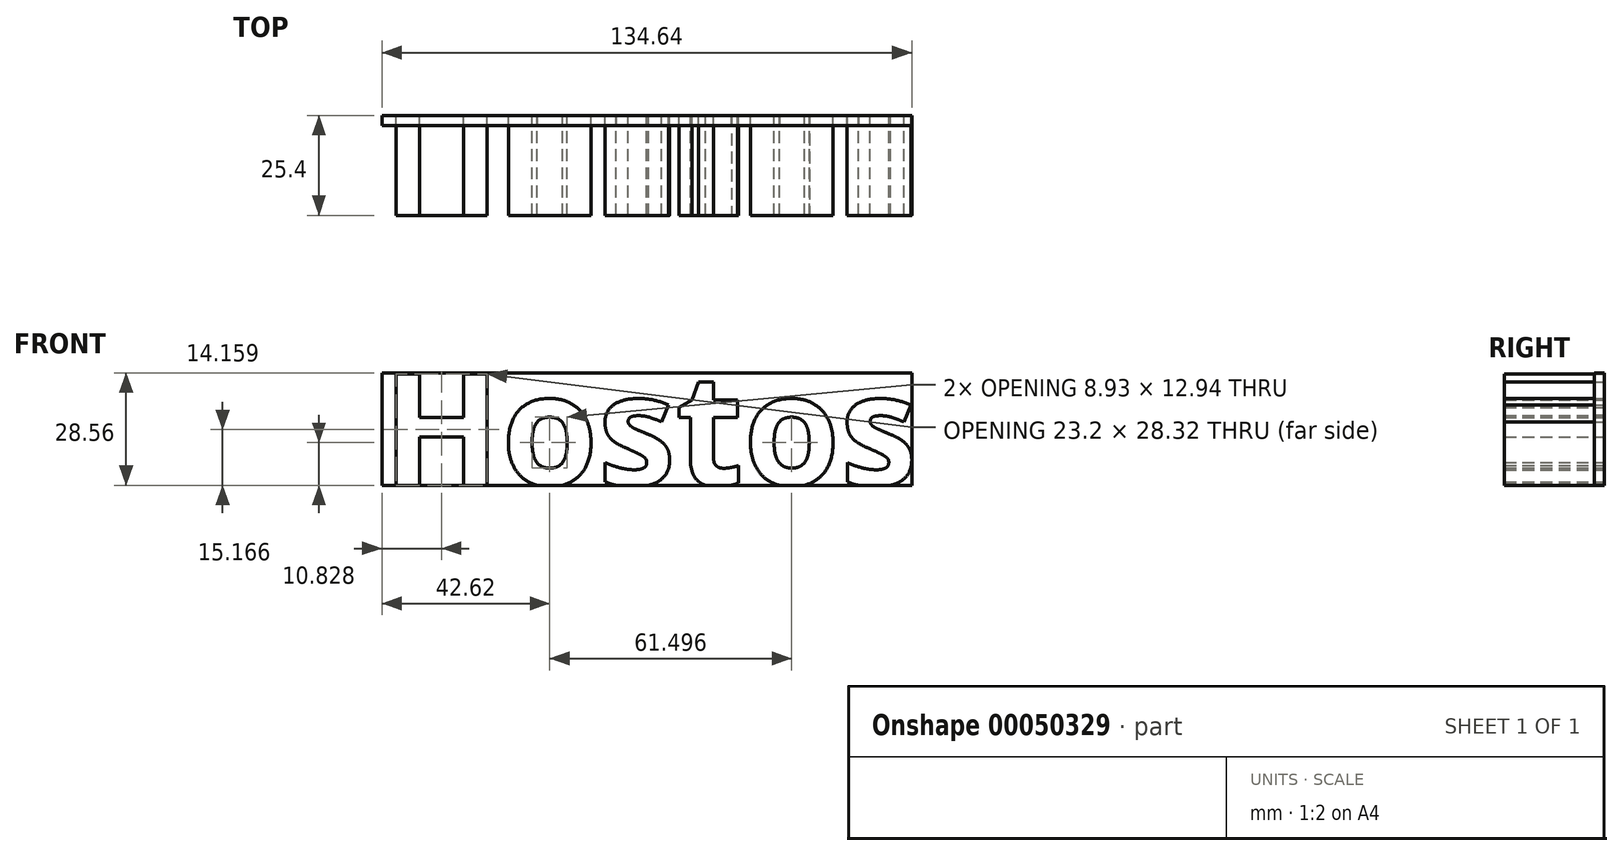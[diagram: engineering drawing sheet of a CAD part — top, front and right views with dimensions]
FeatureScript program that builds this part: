
annotation { "Feature Type Name" : "Feature", "Feature Type Description" : "" }
export const myFeature = defineFeature(function(context is Context, id is Id, definition is map)
    precondition{}
    {
        {
            var Q0;
            Q0=qCreatedBy(makeId("Front.planeOp"),FACE);
            var sketch = newSketch(context, id + "F0", { "sketchPlane" : qUnion([Q0])});
            skText(sketch, "E0", { "text": "Hostos", "fontName": "OpenSans-Bold.ttf"});
            skLineSegment(sketch, "E1.bottom", {"start": v(-52.26, 41.7) * mm, "end": v(82.38, 41.7) * mm});
            skLineSegment(sketch, "E1.top", {"start": v(-52.26, 13.15) * mm, "end": v(82.38, 13.15) * mm});
            skLineSegment(sketch, "E1.left", {"start": v(-52.26, 41.7) * mm, "end": v(-52.26, 13.15) * mm});
            skLineSegment(sketch, "E1.right", {"start": v(82.38, 41.7) * mm, "end": v(82.38, 13.15) * mm});
            skLineSegment(sketch, "E2", {"start": v(-37.26, 25.7) * mm, "end": v(-37.26, 30.35) * mm});
            skLineSegment(sketch, "E3", {"start": v(-14.4, 23.81) * mm, "end": v(-20.07, 23.81) * mm});
            skLineSegment(sketch, "E4", {"start": v(-5.28, 23.64) * mm, "end": v(1.25, 23.64) * mm});
            skLineSegment(sketch, "E5", {"start": v(41.14, 24.33) * mm, "end": v(47.33, 24.33) * mm});
            skLineSegment(sketch, "E6", {"start": v(56.27, 24.5) * mm, "end": v(62.3, 24.5) * mm});
            const initialGuessF0  = {"E0": [-0.05226, 0.01315, 1, 0, 0.02856]};
            skSetInitialGuess(sketch, initialGuessF0);
            skSolve(sketch);
        }
        {
            var Q0;
            {var subQ0=sQuery(id+"F0.wireOp",EDGE,"E0.sketch_text.stroke-1");Q0=makeQuery(id+"F0.imprint","IMPRINT",FACE,{"disambiguationData":[TD([[makeQuery(id+"F0.imprint","IMPRINT",EDGE,{"derivedFrom":subQ0}),-1.0]])]});}
            var Q1;
            Q1=makeQuery(id+"F0.imprint","IMPRINT",FACE,{"disambiguationData":[TD([[makeQuery(id+"F0.imprint","IMPRINT",EDGE,{"derivedFrom":sQuery(id+"F0.wireOp",EDGE,"E0.sketch_text.stroke-12")}),-1.0]])]});
            var Q2;
            {var subQ4=sQuery(id+"F0.wireOp",EDGE,"E0.sketch_text.stroke-30");Q2=makeQuery(id+"F0.imprint","IMPRINT",FACE,{"disambiguationData":[TD([[makeQuery(id+"F0.imprint","IMPRINT",EDGE,{"derivedFrom":subQ4}),-1.0]])]});}
            var Q3;
            Q3=makeQuery(id+"F0.imprint","IMPRINT",FACE,{"disambiguationData":[TD([[makeQuery(id+"F0.imprint","IMPRINT",EDGE,{"derivedFrom":sQuery(id+"F0.wireOp",EDGE,"E0.sketch_text.stroke-56")}),-1.0]])]});
            var Q4;
            Q4=makeQuery(id+"F0.imprint","IMPRINT",FACE,{"disambiguationData":[TD([[makeQuery(id+"F0.imprint","IMPRINT",EDGE,{"derivedFrom":sQuery(id+"F0.wireOp",EDGE,"E0.sketch_text.stroke-74")}),-1.0]])]});
            var Q5;
            {var subQ4=sQuery(id+"F0.wireOp",EDGE,"E0.sketch_text.stroke-92");Q5=makeQuery(id+"F0.imprint","IMPRINT",FACE,{"disambiguationData":[TD([[makeQuery(id+"F0.imprint","IMPRINT",EDGE,{"derivedFrom":subQ4}),-1.0]])]});}
            extrude(context, id + "F1", {"entities" : qUnion([Q0, Q1, Q2, Q3, Q4, Q5]), "depth" : 25.4 * mm});
        }
        {
            var Q0;
            {var subQ25=sQuery(id+"F0.wireOp",EDGE,"E0.sketch_text.stroke-5");Q0=makeQuery(id+"F0.imprint","IMPRINT",FACE,{"disambiguationData":[TD([[makeQuery(id+"F0.imprint","IMPRINT",EDGE,{"derivedFrom":subQ25}),1.0]])]});}
            var Q1;
            {var subQ0=sQuery(id+"F0.wireOp",EDGE,"E0.sketch_text.stroke-1");Q1=makeQuery(id+"F0.imprint","IMPRINT",FACE,{"disambiguationData":[TD([[makeQuery(id+"F0.imprint","IMPRINT",EDGE,{"derivedFrom":subQ0}),1.0]])]});}
            var Q2;
            {var subQ0=sQuery(id+"F0.wireOp",EDGE,"E0.sketch_text.stroke-92");Q2=makeQuery(id+"F0.imprint","IMPRINT",FACE,{"disambiguationData":[TD([[makeQuery(id+"F0.imprint","IMPRINT",EDGE,{"derivedFrom":subQ0}),1.0]])]});}
            var Q3;
            Q3=makeQuery(id+"F0.imprint","IMPRINT",FACE,{"disambiguationData":[TD([[makeQuery(id+"F0.imprint","IMPRINT",EDGE,{"derivedFrom":sQuery(id+"F0.wireOp",EDGE,"E0.sketch_text.stroke-12")}),1.0]])]});
            var Q4;
            Q4=makeQuery(id+"F0.imprint","IMPRINT",FACE,{"disambiguationData":[TD([[makeQuery(id+"F0.imprint","IMPRINT",EDGE,{"derivedFrom":sQuery(id+"F0.wireOp",EDGE,"E0.sketch_text.stroke-74")}),1.0]])]});
            extrude(context, id + "F2", {"entities" : qUnion([Q0, Q1, Q2, Q3, Q4]), "depth" : 2.54 * mm});
        }
    });
